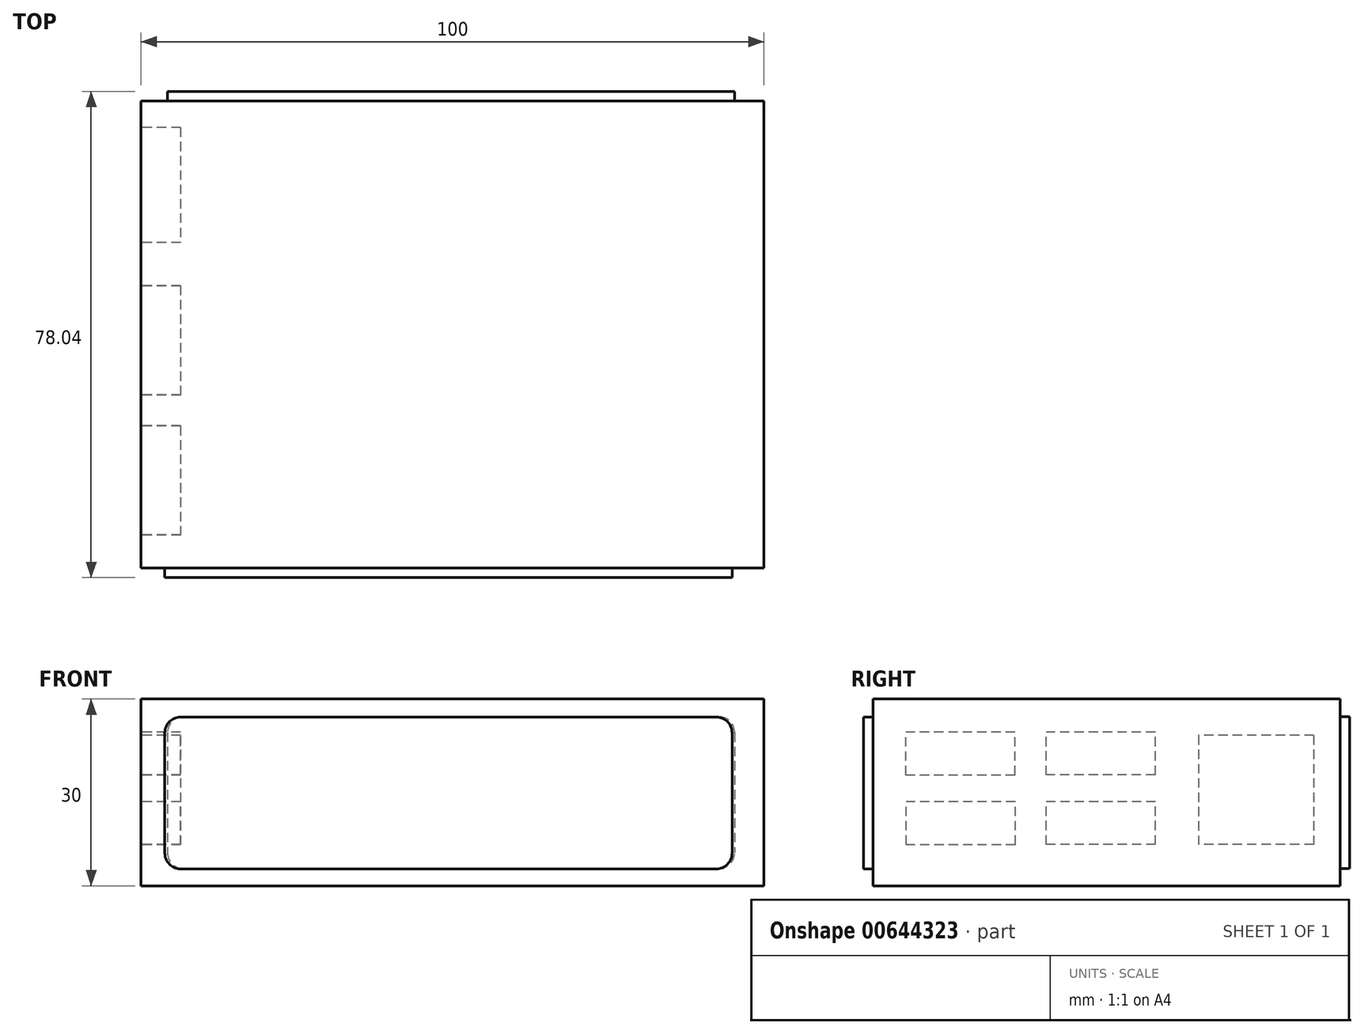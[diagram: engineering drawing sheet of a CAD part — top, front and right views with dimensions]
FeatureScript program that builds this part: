
annotation { "Feature Type Name" : "Feature", "Feature Type Description" : "" }
export const myFeature = defineFeature(function(context is Context, id is Id, definition is map)
    precondition{}
    {
        {
            var Q0;
            Q0=qCreatedBy(makeId("Top.planeOp"),FACE);
            var sketch = newSketch(context, id + "F0", { "sketchPlane" : qUnion([Q0])});
            skLineSegment(sketch, "E0.bottom", {"start": v(-50, 37.5) * mm, "end": v(50, 37.5) * mm});
            skLineSegment(sketch, "E0.top", {"start": v(-50, -37.5) * mm, "end": v(50, -37.5) * mm});
            skLineSegment(sketch, "E0.left", {"start": v(-50, 37.5) * mm, "end": v(-50, -37.5) * mm});
            skLineSegment(sketch, "E0.right", {"start": v(50, 37.5) * mm, "end": v(50, -37.5) * mm});
            skPoint(sketch, "E0.middle", {"position": v(0, 0) * mm});
            skSolve(sketch);
        }
        {
            var Q0;
            Q0=makeQuery(id+"F0.imprint","IMPRINT",FACE,{"disambiguationData":[TD([[makeQuery(id+"F0.imprint","IMPRINT",EDGE,{"derivedFrom":sQuery(id+"F0.wireOp",EDGE,"E0.bottom")}),-1.0]])]});
            extrude(context, id + "F1", {"entities" : qUnion([Q0]), "depth" : 30 * mm});
        }
        {
            var Q0;
            Q0=makeQuery(id+"F1.opExtrude","SWEPT_FACE",FACE,{"disambiguationData":[OSD([sQuery(id+"F0.wireOp",EDGE,"E0.top")])]});
            var sketch = newSketch(context, id + "F2", { "sketchPlane" : qUnion([Q0])});
            skLineSegment(sketch, "E1.bottom", {"start": v(-43.65, 27.1) * mm, "end": v(42.34, 27.1) * mm});
            skLineSegment(sketch, "E1.top", {"start": v(-43.65, 2.7) * mm, "end": v(42.34, 2.7) * mm});
            skLineSegment(sketch, "E1.left", {"start": v(-46.19, 24.57) * mm, "end": v(-46.19, 5.24) * mm});
            skLineSegment(sketch, "E1.right", {"start": v(44.88, 24.57) * mm, "end": v(44.88, 5.24) * mm});
            skPoint(sketch, "E2.visualSharp", {"position": v(-46.19, 27.1) * mm});
            skArc(sketch, "E2.filletArc", {"start": v(-43.65, 27.1) * mm, "mid": v(-45.44, 26.36) * mm, "end": v(-46.19, 24.57) * mm});
            skPoint(sketch, "E3.visualSharp", {"position": v(44.88, 27.1) * mm});
            skArc(sketch, "E3.filletArc", {"start": v(44.88, 24.57) * mm, "mid": v(44.13, 26.36) * mm, "end": v(42.34, 27.1) * mm});
            skPoint(sketch, "E4.visualSharp", {"position": v(-46.19, 2.7) * mm});
            skArc(sketch, "E4.filletArc", {"start": v(-46.19, 5.24) * mm, "mid": v(-45.44, 3.45) * mm, "end": v(-43.65, 2.7) * mm});
            skPoint(sketch, "E5.visualSharp", {"position": v(44.88, 2.7) * mm});
            skArc(sketch, "E5.filletArc", {"start": v(42.34, 2.7) * mm, "mid": v(44.13, 3.45) * mm, "end": v(44.88, 5.24) * mm});
            skSolve(sketch);
        }
        {
            var Q0;
            Q0=makeQuery(id+"F2.imprint","IMPRINT",FACE,{"disambiguationData":[TD([[makeQuery(id+"F2.imprint","IMPRINT",EDGE,{"derivedFrom":sQuery(id+"F2.wireOp",EDGE,"E1.bottom")}),-1.0]])]});
            var Q1;
            Q1=sQuery(id+"F2.wireOp",EDGE,"E1.bottom");
            var Q2;
            Q2=sQuery(id+"F2.wireOp",EDGE,"E2.filletArc");
            var Q3;
            Q3=sQuery(id+"F2.wireOp",EDGE,"E1.left");
            var Q4;
            Q4=sQuery(id+"F2.wireOp",EDGE,"E1.top");
            var Q5;
            Q5=sQuery(id+"F2.wireOp",EDGE,"E4.filletArc");
            extrude(context, id + "F3", {"entities" : qUnion([Q0]), "operationType" : NewBodyOperationType.ADD, "surfaceEntities" : qUnion([Q1, Q2, Q3, Q4, Q5]), "depth" : 1.52 * mm});
        }
        {
            var Q0;
            Q0=makeQuery(id+"F1.opExtrude","SWEPT_FACE",FACE,{"disambiguationData":[OSD([sQuery(id+"F0.wireOp",EDGE,"E0.bottom")])]});
            var sketch = newSketch(context, id + "F4", { "sketchPlane" : qUnion([Q0])});
            skLineSegment(sketch, "E6.bottom", {"start": v(-42.74, 27.15) * mm, "end": v(43.25, 27.15) * mm});
            skLineSegment(sketch, "E6.top", {"start": v(-42.74, 2.75) * mm, "end": v(43.25, 2.75) * mm});
            skLineSegment(sketch, "E6.left", {"start": v(-45.28, 24.61) * mm, "end": v(-45.28, 5.29) * mm});
            skLineSegment(sketch, "E6.right", {"start": v(45.79, 24.61) * mm, "end": v(45.79, 5.29) * mm});
            skPoint(sketch, "E7.visualSharp", {"position": v(-45.28, 27.15) * mm});
            skArc(sketch, "E7.filletArc", {"start": v(-42.74, 27.15) * mm, "mid": v(-44.54, 26.4) * mm, "end": v(-45.28, 24.61) * mm});
            skPoint(sketch, "E8.visualSharp", {"position": v(45.79, 27.15) * mm});
            skArc(sketch, "E8.filletArc", {"start": v(45.79, 24.61) * mm, "mid": v(45.04, 26.4) * mm, "end": v(43.25, 27.15) * mm});
            skPoint(sketch, "E9.visualSharp", {"position": v(-45.28, 2.75) * mm});
            skArc(sketch, "E9.filletArc", {"start": v(-45.28, 5.29) * mm, "mid": v(-44.54, 3.5) * mm, "end": v(-42.74, 2.75) * mm});
            skPoint(sketch, "E10.visualSharp", {"position": v(45.79, 2.75) * mm});
            skArc(sketch, "E10.filletArc", {"start": v(43.25, 2.75) * mm, "mid": v(45.04, 3.5) * mm, "end": v(45.79, 5.29) * mm});
            skSolve(sketch);
        }
        {
            var Q0;
            Q0=qSketchRegion(id+"F4",true);
            extrude(context, id + "F5", {"entities" : qUnion([Q0]), "operationType" : NewBodyOperationType.ADD, "depth" : 1.52 * mm});
        }
        {
            var Q0;
            Q0=makeQuery(id+"F1.opExtrude","SWEPT_FACE",FACE,{"disambiguationData":[OSD([sQuery(id+"F0.wireOp",EDGE,"E0.left")])]});
            var sketch = newSketch(context, id + "F6", { "sketchPlane" : qUnion([Q0])});
            skLineSegment(sketch, "E11.bottom", {"start": v(-33.25, 24.16) * mm, "end": v(-14.74, 24.16) * mm});
            skLineSegment(sketch, "E11.top", {"start": v(-33.25, 6.63) * mm, "end": v(-14.74, 6.63) * mm});
            skLineSegment(sketch, "E11.left", {"start": v(-33.25, 24.16) * mm, "end": v(-33.25, 6.63) * mm});
            skLineSegment(sketch, "E11.right", {"start": v(-14.74, 24.16) * mm, "end": v(-14.74, 6.63) * mm});
            skLineSegment(sketch, "E12.bottom", {"start": v(-7.86, 6.63) * mm, "end": v(9.66, 6.63) * mm});
            skLineSegment(sketch, "E12.top", {"start": v(-7.86, 13.51) * mm, "end": v(9.66, 13.51) * mm});
            skLineSegment(sketch, "E12.left", {"start": v(-7.86, 6.63) * mm, "end": v(-7.86, 13.51) * mm});
            skLineSegment(sketch, "E12.right", {"start": v(9.66, 6.63) * mm, "end": v(9.66, 13.51) * mm});
            skLineSegment(sketch, "E13.bottom", {"start": v(-7.81, 17.8) * mm, "end": v(9.71, 17.8) * mm});
            skLineSegment(sketch, "E13.top", {"start": v(-7.81, 24.69) * mm, "end": v(9.71, 24.69) * mm});
            skLineSegment(sketch, "E13.left", {"start": v(-7.81, 17.8) * mm, "end": v(-7.81, 24.69) * mm});
            skLineSegment(sketch, "E13.right", {"start": v(9.71, 17.8) * mm, "end": v(9.71, 24.69) * mm});
            skLineSegment(sketch, "E14.bottom", {"start": v(14.65, 6.6) * mm, "end": v(32.18, 6.6) * mm});
            skLineSegment(sketch, "E14.top", {"start": v(14.65, 13.49) * mm, "end": v(32.18, 13.49) * mm});
            skLineSegment(sketch, "E14.left", {"start": v(14.65, 6.6) * mm, "end": v(14.65, 13.49) * mm});
            skLineSegment(sketch, "E14.right", {"start": v(32.18, 6.6) * mm, "end": v(32.18, 13.49) * mm});
            skLineSegment(sketch, "E15.bottom", {"start": v(14.7, 17.78) * mm, "end": v(32.23, 17.78) * mm});
            skLineSegment(sketch, "E15.top", {"start": v(14.7, 24.66) * mm, "end": v(32.23, 24.66) * mm});
            skLineSegment(sketch, "E15.left", {"start": v(14.7, 17.78) * mm, "end": v(14.7, 24.66) * mm});
            skLineSegment(sketch, "E15.right", {"start": v(32.23, 17.78) * mm, "end": v(32.23, 24.66) * mm});
            skSolve(sketch);
        }
        {
            var Q0;
            Q0=qSketchRegion(id+"F6",true);
            extrude(context, id + "F7", {"entities" : qUnion([Q0]), "operationType" : NewBodyOperationType.REMOVE, "oppositeDirection" : true, "depth" : 6.35 * mm});
        }
    });
